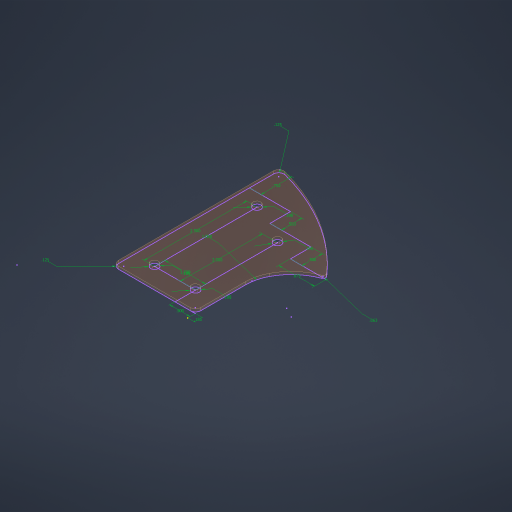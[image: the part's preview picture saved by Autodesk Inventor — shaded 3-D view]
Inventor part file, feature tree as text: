
AUTODESK INVENTOR PART (.ipt)
format: ipt  version: 2024 (Build 280153000, 153)  size: 250,880 bytes
history: native  units: in
note: dims shown in document units (in); Inventor stores cm internally (conversion verified against a paired STEP export)
features: sketch x1, extrude x1
ambient origin geometry x8: Origin, YZ Plane, XZ Plane, XY Plane, X Axis, Y Axis, Z Axis, Center Point
bodies: Solid1 (feature_tree)
feature tree (2):
  sketch  "Sketch2"  dims[d3=0.5in d4=0.75in d5=0.5in d6=0.875in d8=0.0625in d9=0.0in d18=0.125in d19=0.0625in d20=1.0in d23=0.185in d24=0.5in d25=1.0in d26=2.5in d27=2.0in d28=0.125in d29=0.1875in d30=0.1875in d31=0.1875in d32=0.1875in]
  extrude  "Extrusion1"  Depth=0.125in
